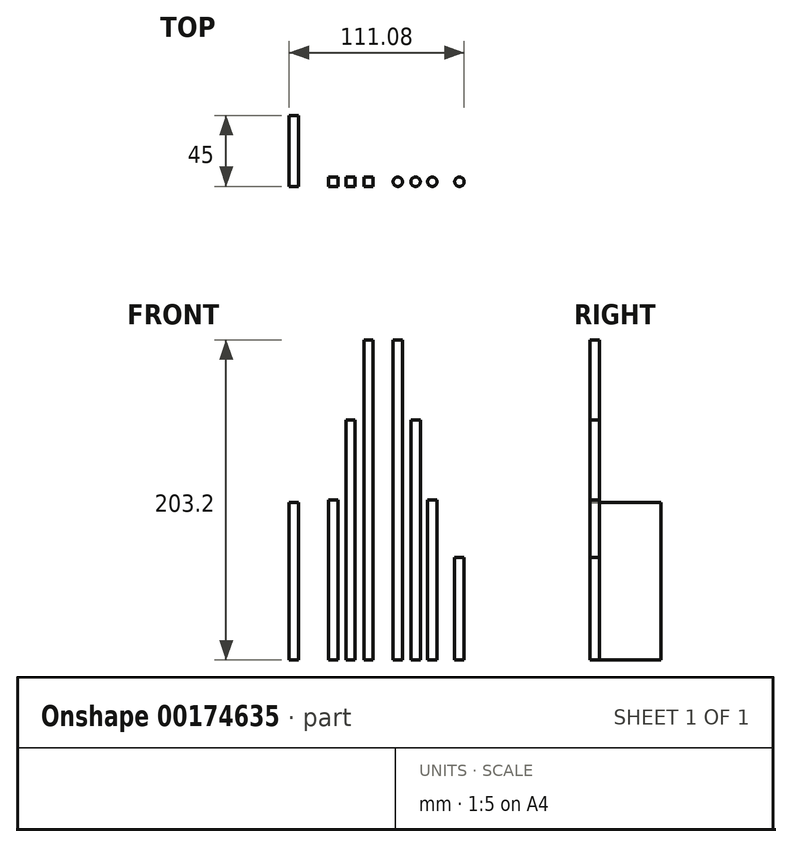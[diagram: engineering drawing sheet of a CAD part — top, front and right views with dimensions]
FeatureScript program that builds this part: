
annotation { "Feature Type Name" : "Feature", "Feature Type Description" : "" }
export const myFeature = defineFeature(function(context is Context, id is Id, definition is map)
    precondition{}
    {
        {
            var Q0;
            Q0=qCreatedBy(makeId("Top.planeOp"),FACE);
            var sketch = newSketch(context, id + "F0", { "sketchPlane" : qUnion([Q0])});
            skLineSegment(sketch, "E0.bottom", {"start": v(-7.87, 0) * mm, "end": v(-13.87, 0) * mm});
            skLineSegment(sketch, "E0.top", {"start": v(-7.87, 6) * mm, "end": v(-13.87, 6) * mm});
            skLineSegment(sketch, "E0.left", {"start": v(-7.87, 0) * mm, "end": v(-7.87, 6) * mm});
            skLineSegment(sketch, "E0.right", {"start": v(-13.87, 0) * mm, "end": v(-13.87, 6) * mm});
            skLineSegment(sketch, "E1.bottom", {"start": v(-19.3, 0) * mm, "end": v(-25.3, 0) * mm});
            skLineSegment(sketch, "E1.top", {"start": v(-19.3, 6) * mm, "end": v(-25.3, 6) * mm});
            skLineSegment(sketch, "E1.left", {"start": v(-19.3, 0) * mm, "end": v(-19.3, 6) * mm});
            skLineSegment(sketch, "E1.right", {"start": v(-25.3, 0) * mm, "end": v(-25.3, 6) * mm});
            skLineSegment(sketch, "E2.bottom", {"start": v(-30.15, 0) * mm, "end": v(-36.15, 0) * mm});
            skLineSegment(sketch, "E2.top", {"start": v(-30.15, 6) * mm, "end": v(-36.15, 6) * mm});
            skLineSegment(sketch, "E2.left", {"start": v(-30.15, 0) * mm, "end": v(-30.15, 6) * mm});
            skLineSegment(sketch, "E2.right", {"start": v(-36.15, 0) * mm, "end": v(-36.15, 6) * mm});
            skPoint(sketch, "E3.endSnap0", {"position": v(-7.87, 3) * mm});
            skCircle(sketch, "E4", {"center": v(7.77, 3) * mm, "radius": 3 * mm});
            skCircle(sketch, "E5", {"center": v(19.04, 3) * mm, "radius": 3 * mm});
            skCircle(sketch, "E6", {"center": v(46.88, 3) * mm, "radius": 3 * mm});
            skLineSegment(sketch, "E7", {"start": v(-7.87, 3) * mm, "end": v(78.63, 3) * mm, "construction": true});
            skCircle(sketch, "E8", {"center": v(29.67, 3) * mm, "radius": 3 * mm});
            skLineSegment(sketch, "E9.bottom", {"start": v(-55.2, 0) * mm, "end": v(-61.2, 0) * mm});
            skLineSegment(sketch, "E9.top", {"start": v(-55.2, 45) * mm, "end": v(-61.2, 45) * mm});
            skLineSegment(sketch, "E9.left", {"start": v(-55.2, 0) * mm, "end": v(-55.2, 45) * mm});
            skLineSegment(sketch, "E9.right", {"start": v(-61.2, 0) * mm, "end": v(-61.2, 45) * mm});
            skSolve(sketch);
        }
        {
            var Q0;
            Q0=makeQuery(id+"F0.imprint","IMPRINT",FACE,{"disambiguationData":[TD([[makeQuery(id+"F0.imprint","IMPRINT",EDGE,{"derivedFrom":sQuery(id+"F0.wireOp",EDGE,"E2.bottom")}),-1.0]])]});
            extrude(context, id + "F1", {"entities" : qUnion([Q0]), "depth" : 101.6 * mm});
        }
        {
            var Q0;
            Q0=makeQuery(id+"F0.imprint","IMPRINT",FACE,{"disambiguationData":[TD([[makeQuery(id+"F0.imprint","IMPRINT",EDGE,{"derivedFrom":sQuery(id+"F0.wireOp",EDGE,"E1.bottom")}),-1.0]])]});
            extrude(context, id + "F2", {"entities" : qUnion([Q0]), "depth" : 152.4 * mm});
        }
        {
            var Q0;
            Q0=makeQuery(id+"F0.imprint","IMPRINT",FACE,{"disambiguationData":[TD([[makeQuery(id+"F0.imprint","IMPRINT",EDGE,{"derivedFrom":sQuery(id+"F0.wireOp",EDGE,"E0.bottom")}),-1.0]])]});
            extrude(context, id + "F3", {"entities" : qUnion([Q0]), "depth" : 203.2 * mm});
        }
        {
            var Q0;
            Q0=makeQuery(id+"F0.imprint","IMPRINT",FACE,{"disambiguationData":[TD([[makeQuery(id+"F0.imprint","IMPRINT",EDGE,{"derivedFrom":sQuery(id+"F0.wireOp",EDGE,"E4")}),1.0]])]});
            extrude(context, id + "F4", {"entities" : qUnion([Q0]), "depth" : 203.2 * mm});
        }
        {
            var Q0;
            Q0=makeQuery(id+"F0.imprint","IMPRINT",FACE,{"disambiguationData":[TD([[makeQuery(id+"F0.imprint","IMPRINT",EDGE,{"derivedFrom":sQuery(id+"F0.wireOp",EDGE,"E5")}),1.0]])]});
            extrude(context, id + "F5", {"entities" : qUnion([Q0]), "depth" : 152.4 * mm});
        }
        {
            var Q0;
            Q0=makeQuery(id+"F0.imprint","IMPRINT",FACE,{"disambiguationData":[TD([[makeQuery(id+"F0.imprint","IMPRINT",EDGE,{"derivedFrom":sQuery(id+"F0.wireOp",EDGE,"E8")}),1.0]])]});
            extrude(context, id + "F6", {"entities" : qUnion([Q0]), "depth" : 101.6 * mm});
        }
        {
            var Q0;
            Q0=makeQuery(id+"F0.imprint","IMPRINT",FACE,{"disambiguationData":[TD([[makeQuery(id+"F0.imprint","IMPRINT",EDGE,{"derivedFrom":sQuery(id+"F0.wireOp",EDGE,"E6")}),1.0]])]});
            extrude(context, id + "F7", {"entities" : qUnion([Q0]), "depth" : 65 * mm});
        }
        {
            var Q0;
            Q0=makeQuery(id+"F0.imprint","IMPRINT",FACE,{"disambiguationData":[TD([[makeQuery(id+"F0.imprint","IMPRINT",EDGE,{"derivedFrom":sQuery(id+"F0.wireOp",EDGE,"E9.bottom")}),-1.0]])]});
            extrude(context, id + "F8", {"entities" : qUnion([Q0]), "depth" : 100 * mm});
        }
    });
